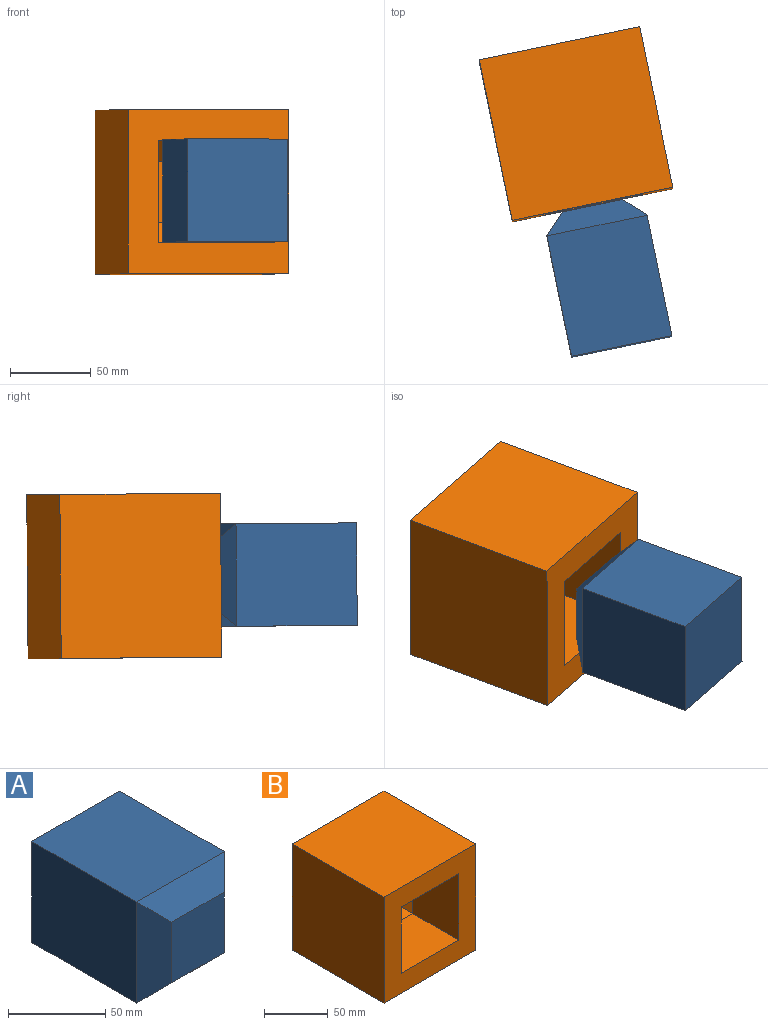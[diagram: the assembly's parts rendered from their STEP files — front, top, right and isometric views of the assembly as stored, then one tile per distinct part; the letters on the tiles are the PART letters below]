
ASSEMBLY  parts=2 mates=1
PART A: 10 faces, bbox 63.5x88.9x63.5 mm
  f0: plane 76.2x63.5mm, normal (0,0,1), area 4838.7mm2, adj f1,f3,f5,f6
  f1: plane 76.2x63.5mm, normal (-1,0,0), area 4838.7mm2, adj f0,f2,f5,f7
  f2: plane 76.2x63.5mm, normal (0,0,-1), area 4838.7mm2, adj f1,f3,f5,f9
  f3: plane 76.2x63.5mm, normal (1,0,0), area 4838.7mm2, adj f0,f2,f5,f8
  f4: plane 38.1x38.1mm, normal (0,-1,0), area 1451.6mm2, adj f6,f7,f8,f9
  f5: plane 63.5x63.5mm, normal (0,1,0), area 4032.3mm2, adj f0,f1,f2,f3
  f6: plane 63.5x12.7mm, normal (0,-0.71,0.71), area 912.4mm2, adj f0,f4,f7,f8
  f7: plane 63.5x12.7mm, normal (-0.71,-0.71,0), area 912.4mm2, adj f1,f4,f6,f9
  f8: plane 63.5x12.7mm, normal (0.71,-0.71,0), area 912.4mm2, adj f3,f4,f6,f9
  f9: plane 63.5x12.7mm, normal (0,-0.71,-0.71), area 912.4mm2, adj f2,f4,f7,f8
PART B: 15 faces, bbox 101.6x101.6x101.6 mm
  f0: plane 101.6x101.6mm, normal (0,-1,0), area 6290.3mm2, adj f1,f2,f3,f4,f6,f7,f8,f9
  f1: plane 101.6x101.6mm, normal (1,0,0), area 10322.6mm2, adj f0,f2,f4,f5
  f2: plane 101.6x101.6mm, normal (0,0,1), area 10322.6mm2, adj f0,f1,f3,f5
  f3: plane 101.6x101.6mm, normal (-1,0,0), area 10322.6mm2, adj f0,f2,f4,f5
  f4: plane 101.6x101.6mm, normal (0,0,-1), area 10322.6mm2, adj f0,f1,f3,f5
  f5: plane 101.6x101.6mm, normal (0,1,0), area 10322.6mm2, adj f1,f2,f3,f4
  f6: plane 63.5x50.8mm, normal (0,0,-1), area 3225.8mm2, adj f0,f7,f9,f12
  f7: plane 63.5x50.8mm, normal (1,0,0), area 3225.8mm2, adj f0,f6,f8,f11
  f8: plane 63.5x50.8mm, normal (0,0,1), area 3225.8mm2, adj f0,f7,f9,f13
  f9: plane 63.5x50.8mm, normal (-1,0,0), area 3225.8mm2, adj f0,f6,f8,f14
  f10: plane 38.1x38.1mm, normal (0,-1,0), area 1451.6mm2, adj f11,f12,f13,f14
  f11: plane 63.5x12.7mm, normal (0.71,-0.71,0), area 912.4mm2, adj f7,f10,f12,f13
  f12: plane 63.5x12.7mm, normal (0,-0.71,-0.71), area 912.4mm2, adj f6,f10,f11,f14
  f13: plane 63.5x12.7mm, normal (0,-0.71,0.71), area 912.4mm2, adj f8,f10,f11,f14
  f14: plane 63.5x12.7mm, normal (-0.71,-0.71,0), area 912.4mm2, adj f9,f10,f12,f13
PLACE A rot(axis=(0,0,-1),168.4deg) t=(26.16,-177.24,8.13)mm
PLACE B rot(axis=(0.1,-0.99,0),179.9deg) t=(-19.34,8.85,10.92)mm
MATE slider B.f10 <-> A.f4  axis (0.2,-0.98,0.01) through (0.46,-26.03,3.17)mm
